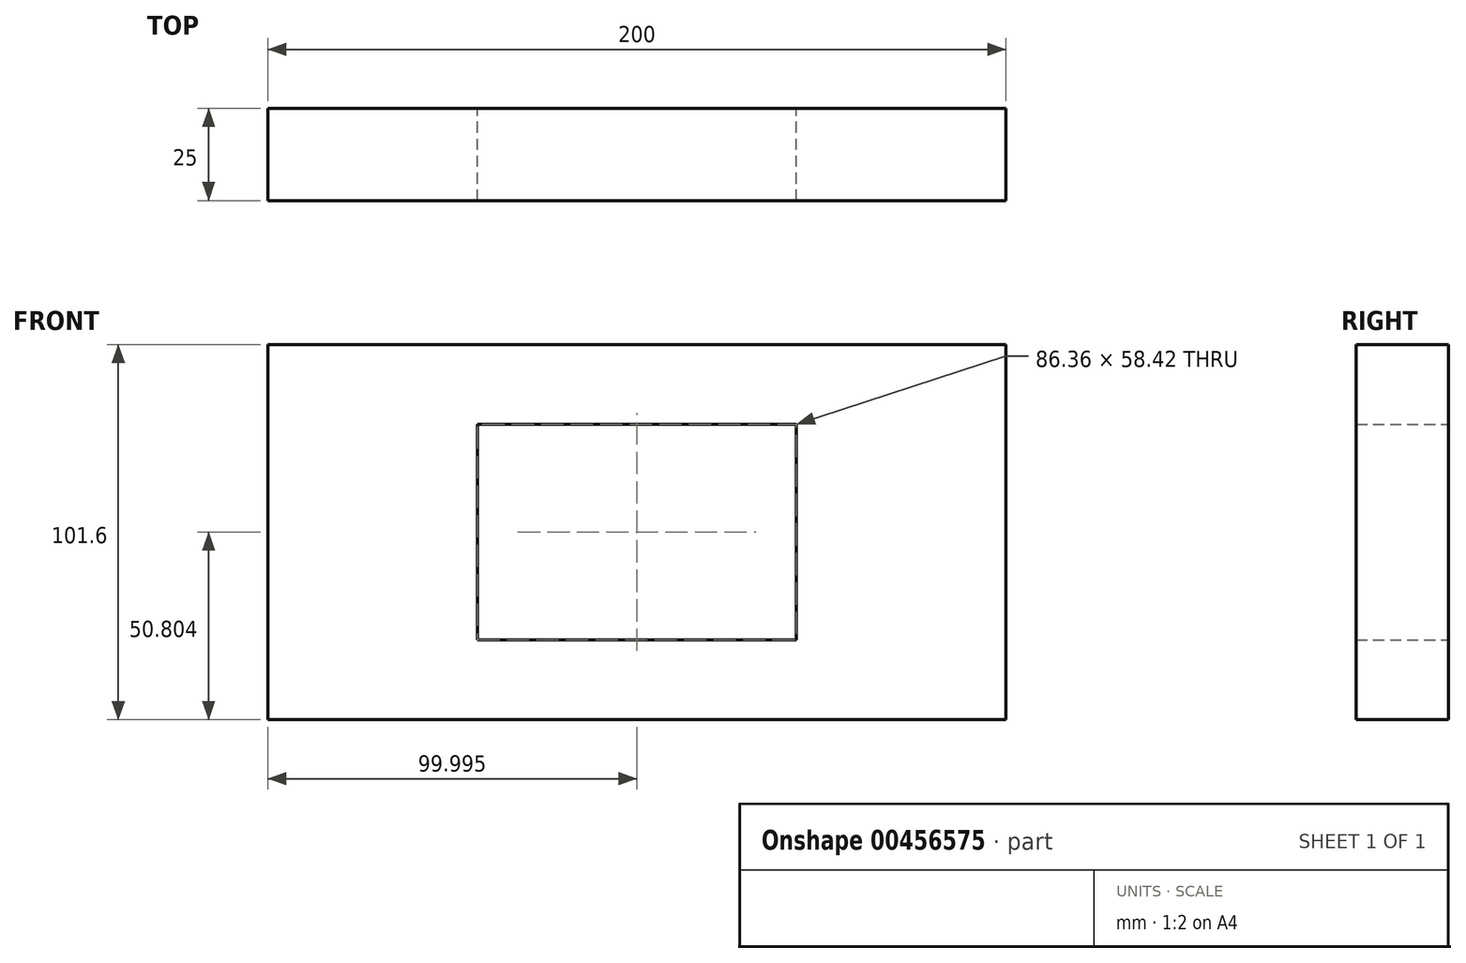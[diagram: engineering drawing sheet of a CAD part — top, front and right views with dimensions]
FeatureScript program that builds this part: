
annotation { "Feature Type Name" : "Feature", "Feature Type Description" : "" }
export const myFeature = defineFeature(function(context is Context, id is Id, definition is map)
    precondition{}
    {
        {
            var Q0;
            Q0=qCreatedBy(makeId("Front.planeOp"),FACE);
            var sketch = newSketch(context, id + "F0", { "sketchPlane" : qUnion([Q0])});
            skLineSegment(sketch, "E0.bottom", {"start": v(-103, 71.64) * mm, "end": v(97, 71.64) * mm});
            skLineSegment(sketch, "E0.top", {"start": v(-103, -29.96) * mm, "end": v(97, -29.96) * mm});
            skLineSegment(sketch, "E0.left", {"start": v(-103, 71.64) * mm, "end": v(-103, -29.96) * mm});
            skLineSegment(sketch, "E0.right", {"start": v(97, 71.64) * mm, "end": v(97, -29.96) * mm});
            skLineSegment(sketch, "E1.bottom", {"start": v(-46.18, 50.05) * mm, "end": v(40.18, 50.05) * mm});
            skLineSegment(sketch, "E1.top", {"start": v(-46.18, -8.37) * mm, "end": v(40.18, -8.37) * mm});
            skLineSegment(sketch, "E1.left", {"start": v(-46.18, 50.05) * mm, "end": v(-46.18, -8.37) * mm});
            skLineSegment(sketch, "E1.right", {"start": v(40.18, 50.05) * mm, "end": v(40.18, -8.37) * mm});
            skSolve(sketch);
        }
        {
            var Q0;
            Q0=makeQuery(id+"F0.imprint","IMPRINT",FACE,{"disambiguationData":[TD([[makeQuery(id+"F0.imprint","IMPRINT",EDGE,{"derivedFrom":sQuery(id+"F0.wireOp",EDGE,"E0.bottom")}),-1.0]])]});
            extrude(context, id + "F1", {"entities" : qUnion([Q0]), "depth" : 25 * mm});
        }
        {
            var Q0;
            Q0=makeQuery(id+"F0.imprint","IMPRINT",FACE,{"disambiguationData":[TD([[makeQuery(id+"F0.imprint","IMPRINT",EDGE,{"derivedFrom":sQuery(id+"F0.wireOp",EDGE,"E1.bottom")}),-1.0]])]});
            extrude(context, id + "F2", {"entities" : qUnion([Q0]), "operationType" : NewBodyOperationType.REMOVE, "depth" : 25 * mm});
        }
    });
